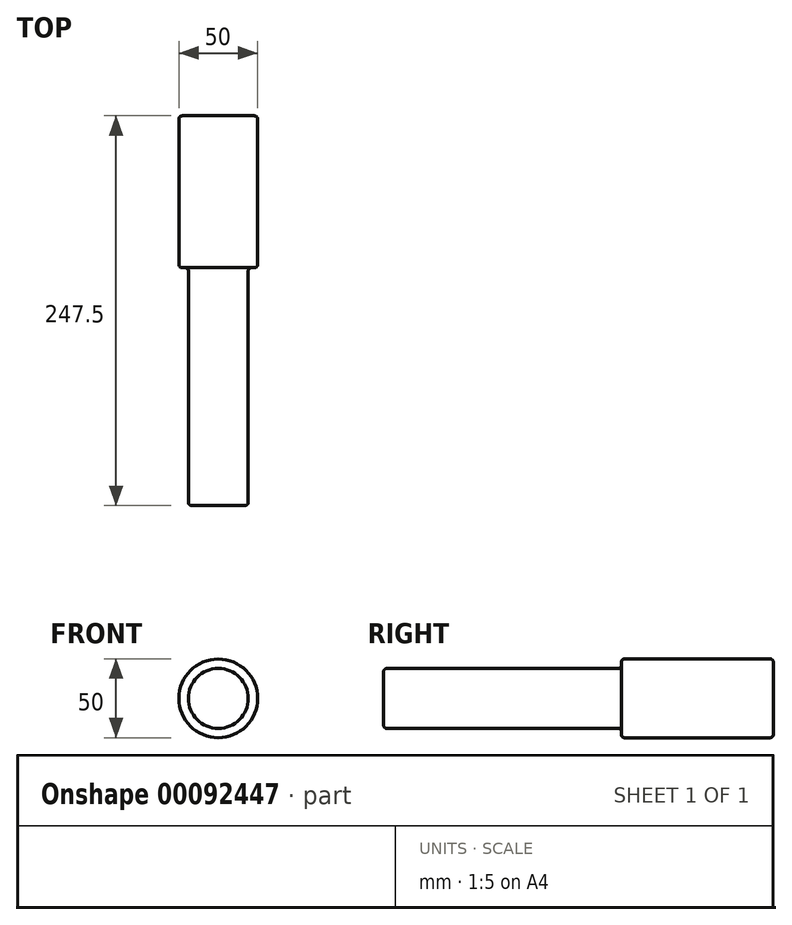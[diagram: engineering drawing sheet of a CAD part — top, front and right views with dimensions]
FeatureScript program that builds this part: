
annotation { "Feature Type Name" : "Feature", "Feature Type Description" : "" }
export const myFeature = defineFeature(function(context is Context, id is Id, definition is map)
    precondition{}
    {
        {
            var Q0;
            Q0=qCreatedBy(makeId("Front.planeOp"),FACE);
            var sketch = newSketch(context, id + "F0", { "sketchPlane" : qUnion([Q0])});
            skCircle(sketch, "E0", {"center": v(0, 0) * mm, "radius": 19 * mm});
            skSolve(sketch);
        }
        {
            var Q0;
            Q0 = qSketchRegion(id + "F0", true);
            extrude(context, id + "F1", {"entities" : qUnion([Q0]), "depth" : 151 * mm});
        }
        {
            var Q0;
            Q0=qCreatedBy(makeId("Front.planeOp"),FACE);
            var sketch = newSketch(context, id + "F2", { "sketchPlane" : qUnion([Q0])});
            skCircle(sketch, "E1", {"center": v(-0.02, 0.06) * mm, "radius": 25 * mm});
            skSolve(sketch);
        }
        {
            var Q0;
            Q0 = qSketchRegion(id + "F2", true);
            extrude(context, id + "F3", {"entities" : qUnion([Q0]), "operationType" : NewBodyOperationType.ADD, "oppositeDirection" : true, "depth" : 96.5 * mm});
        }
        {
            var Q0;
            Q0=makeQuery(id+"F1.opExtrude","CAP_EDGE",EDGE,{"disambiguationData":[OSD([sQuery(id+"F0.wireOp",EDGE,"E0")])],"isStart":false});
            var Q1;
            Q1=makeQuery(id+"F1.opExtrude","SWEPT_FACE",FACE,{"disambiguationData":[OSD([sQuery(id+"F0.wireOp",EDGE,"E0")])]});
            var Q2;
            Q2=makeQuery(id+"F3.opExtrude","CAP_EDGE",EDGE,{"disambiguationData":[OSD([sQuery(id+"F2.wireOp",EDGE,"E1")])],"isStart":true});
            var Q3;
            Q3=makeQuery(id+"F3.opExtrude","CAP_EDGE",EDGE,{"disambiguationData":[OSD([sQuery(id+"F2.wireOp",EDGE,"E1")])],"isStart":false});
            var Q4;
            Q4=makeQuery(id+"F1.opExtrude","CAP_EDGE",EDGE,{"disambiguationData":[OSD([sQuery(id+"F0.wireOp",EDGE,"E0")])],"isStart":true});
            fillet(context, id + "F4", {"entities" : qUnion([Q0, Q1, Q2, Q3, Q4]), "radius" : 2 * mm, "tangentPropagation" : true, "allowEdgeOverflow" : false});
        }
    });
